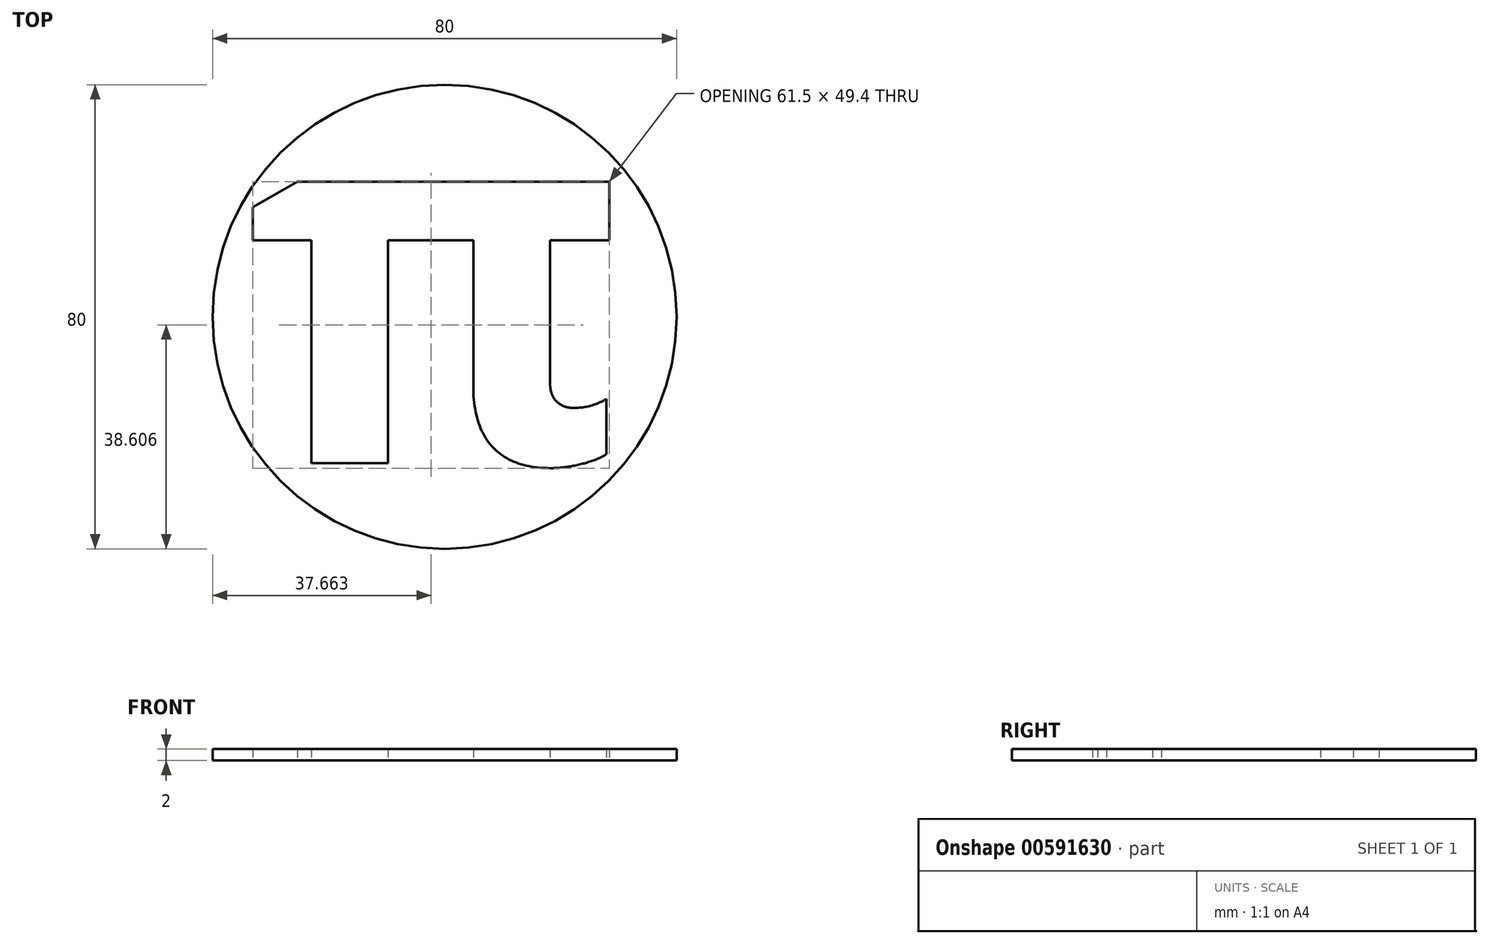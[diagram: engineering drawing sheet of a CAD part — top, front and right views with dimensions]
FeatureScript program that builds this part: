
annotation { "Feature Type Name" : "Feature", "Feature Type Description" : "" }
export const myFeature = defineFeature(function(context is Context, id is Id, definition is map)
    precondition{}
    {
        {
            var Q0;
            Q0=qCreatedBy(makeId("Top.planeOp"),FACE);
            var sketch = newSketch(context, id + "F0", { "sketchPlane" : qUnion([Q0])});
            skCircle(sketch, "E0", {"center": v(0, 0) * mm, "radius": 40 * mm});
            skText(sketch, "E1", { "text": "π", "fontName": "OpenSans-Bold.ttf"});
            skPoint(sketch, "E2", {"position": v(-206.68, 110.79) * mm});
            const initialGuessF0  = {"E1": [-0.03417, -0.02522, 1, 0, 0.064]};
            skSetInitialGuess(sketch, initialGuessF0);
            skSolve(sketch);
        }
        {
            var Q0;
            Q0=makeQuery(id+"F0.imprint","IMPRINT",FACE,{"disambiguationData":[TD([[makeQuery(id+"F0.imprint","IMPRINT",EDGE,{"derivedFrom":sQuery(id+"F0.wireOp",EDGE,"E0")}),1.0]])]});
            extrude(context, id + "F1", {"entities" : qUnion([Q0]), "depth" : 2 * mm, "offsetDistance" : 25 * mm});
        }
    });
